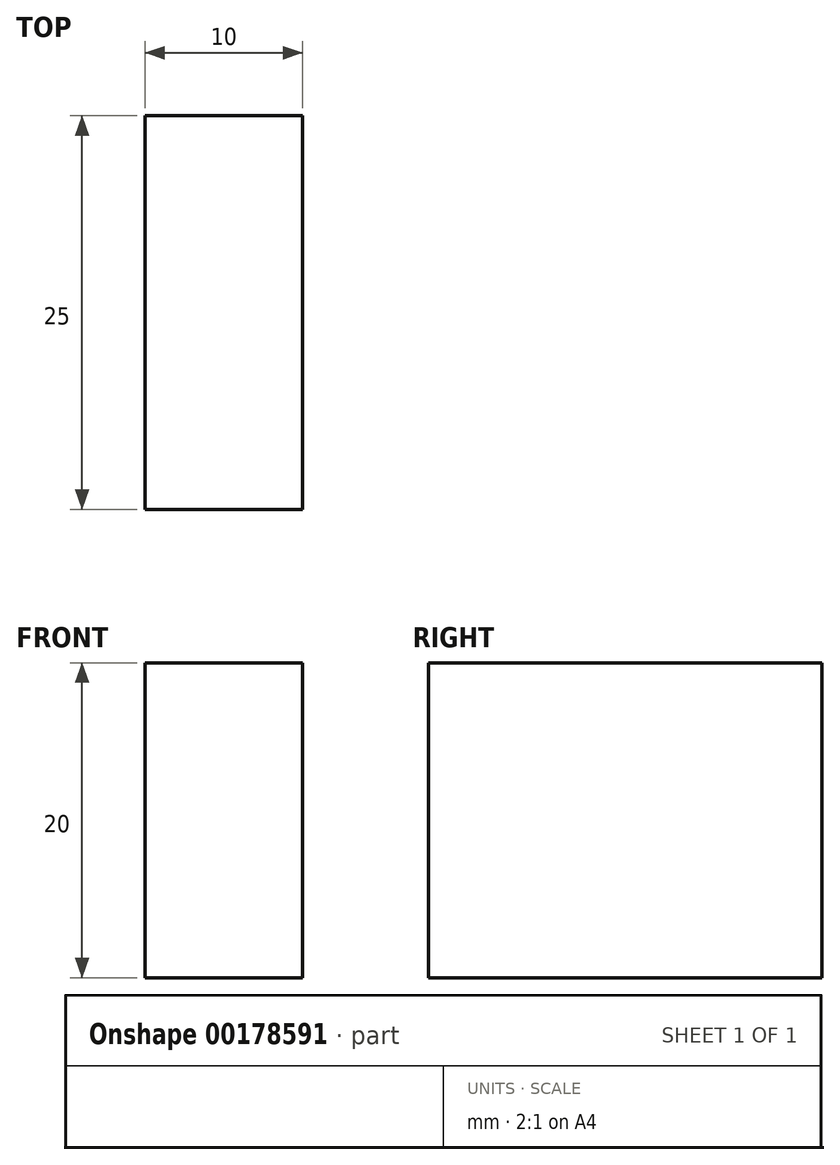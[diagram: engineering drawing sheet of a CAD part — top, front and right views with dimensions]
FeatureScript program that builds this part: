
annotation { "Feature Type Name" : "Feature", "Feature Type Description" : "" }
export const myFeature = defineFeature(function(context is Context, id is Id, definition is map)
    precondition{}
    {
        {
            var Q0;
            Q0=qCreatedBy(makeId("Front.planeOp"),FACE);
            var sketch = newSketch(context, id + "F0", { "sketchPlane" : qUnion([Q0])});
            skLineSegment(sketch, "E0.bottom", {"start": v(-49.17, 16.86) * mm, "end": v(-39.17, 16.86) * mm});
            skLineSegment(sketch, "E0.top", {"start": v(-49.17, -3.14) * mm, "end": v(-39.17, -3.14) * mm});
            skLineSegment(sketch, "E0.left", {"start": v(-49.17, 16.86) * mm, "end": v(-49.17, -3.14) * mm});
            skLineSegment(sketch, "E0.right", {"start": v(-39.17, 16.86) * mm, "end": v(-39.17, -3.14) * mm});
            skSolve(sketch);
        }
        {
            var Q0;
            Q0=makeQuery(id+"F0.imprint","IMPRINT",FACE,{"disambiguationData":[TD([[makeQuery(id+"F0.imprint","IMPRINT",EDGE,{"derivedFrom":sQuery(id+"F0.wireOp",EDGE,"E0.bottom")}),-1.0]])]});
            extrude(context, id + "F1", {"entities" : qUnion([Q0]), "depth" : 25 * mm});
        }
    });
